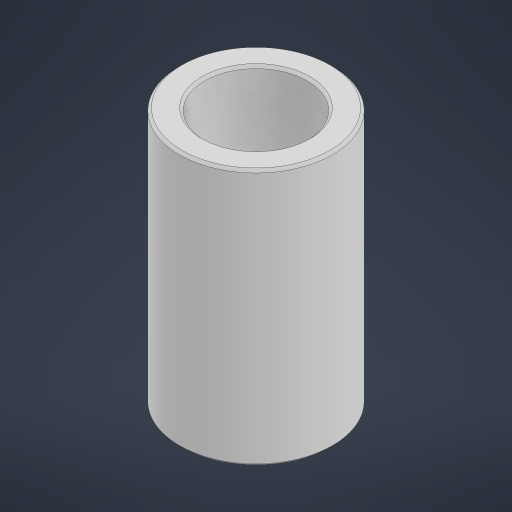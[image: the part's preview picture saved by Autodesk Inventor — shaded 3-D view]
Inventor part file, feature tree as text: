
AUTODESK INVENTOR PART (.ipt)
format: ipt  version: 2023 (Build 270158000, 158)  size: 174,592 bytes
history: native  units: in
note: dims shown in document units (in); Inventor stores cm internally (conversion verified against a paired STEP export)
features: chamfer x1
ambient origin geometry x8: Origin, YZ Plane, XZ Plane, XY Plane, X Axis, Y Axis, Z Axis, Center Point
bodies: Solid1 (feature_tree)
feature tree (1):
  chamfer  "Chamfer1"  [1 undecoded]
note: 1 required parameter value undecoded (feature->parameter linkage not recoverable at this tier; creation-order binding heuristic only, values carry confidence <= 0.55)
